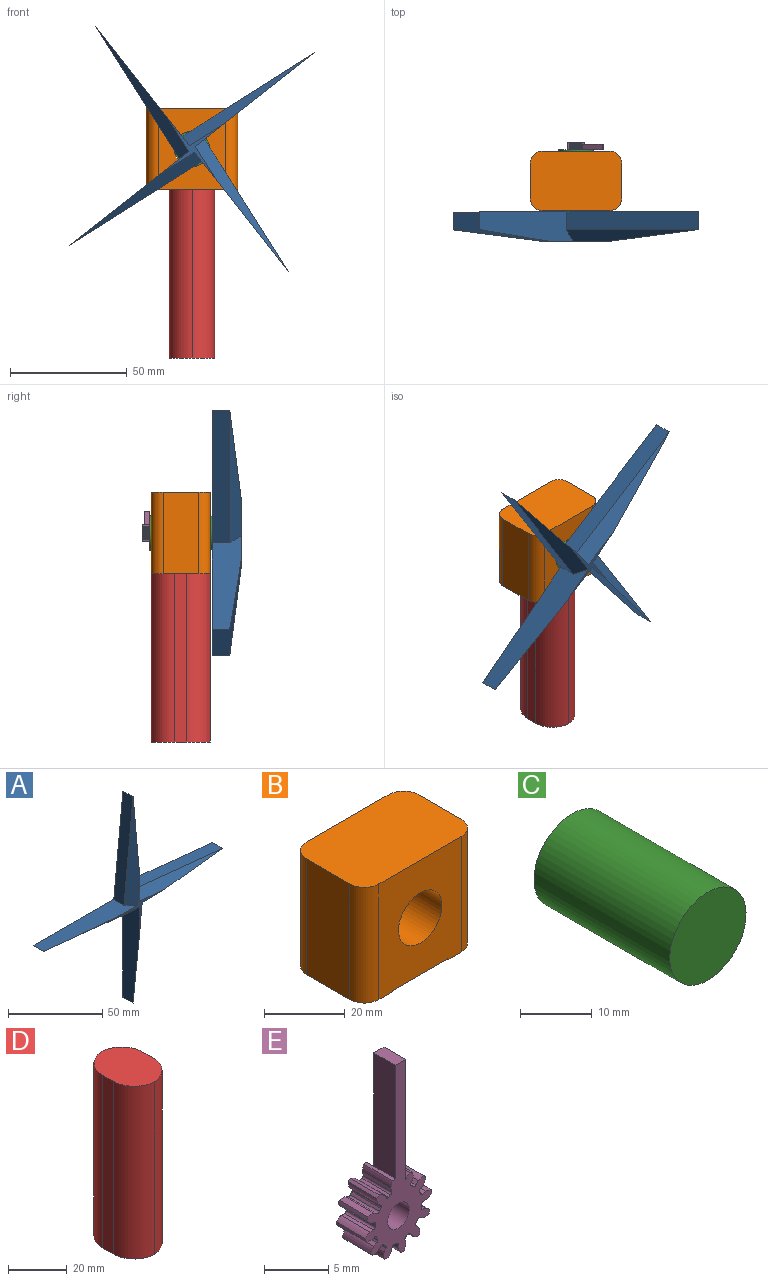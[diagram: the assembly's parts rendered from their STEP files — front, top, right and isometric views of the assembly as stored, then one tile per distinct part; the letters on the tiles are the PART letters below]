
ASSEMBLY  parts=5 mates=4
PART A: 14 faces, bbox 134x12.7x134 mm
  f0: plane 66.98x7.62mm, normal (-0.99,0,0.1), area 513.1mm2, adj f1,f7,f9,f13
  f1: plane 65.2x12.7mm, normal (0,0,1), area 650mm2, adj f0,f2,f8,f9,f12,f13
  f2: plane 66.98x7.62mm, normal (-0.1,0,-0.99), area 513.1mm2, adj f1,f3,f9,f12
  f3: plane 65.2x12.7mm, normal (-1,0,0), area 650mm2, adj f2,f4,f8,f9,f11,f12
  f4: plane 66.98x7.62mm, normal (0.99,0,-0.1), area 513.1mm2, adj f3,f5,f9,f11
  f5: plane 65.2x12.7mm, normal (0,0,-1), area 650mm2, adj f4,f6,f8,f9,f10,f11
  f6: plane 66.98x7.62mm, normal (0.1,0,0.99), area 513.1mm2, adj f5,f7,f9,f10
  f7: plane 65.2x12.7mm, normal (1,0,0), area 650mm2, adj f0,f6,f8,f9,f10,f13
  f8: plane 34.58x34.58mm, normal (0,-1,0), area 61.4mm2, adj f1,f3,f5,f7,f10,f11,f12,f13
  f9: plane 133.96x133.96mm, normal (0,1,0), area 922.1mm2, adj f0,f1,f2,f3,f4,f5,f6,f7
  f10: plane 66.98x6.88mm, normal (0.07,-0.71,0.7), area 304.3mm2, adj f5,f6,f7,f8
  f11: plane 66.98x6.88mm, normal (0.7,-0.71,-0.07), area 304.3mm2, adj f3,f4,f5,f8
  f12: plane 66.98x6.88mm, normal (-0.07,-0.71,-0.7), area 304.3mm2, adj f1,f2,f3,f8
  f13: plane 66.98x6.88mm, normal (-0.7,-0.71,0.07), area 304.3mm2, adj f0,f1,f7,f8
PART B: 15 faces, bbox 39.1x25.4x35.1 mm
  f0: plane 25.4x19.4mm, normal (0,0,-1), area 492.9mm2, adj f1,f7,f8,f9
  f1: plane 25.4x0.27mm, normal (-1,0,0), area 6.8mm2, adj f0,f2,f8,f9
  f2: plane 25.4x9.84mm, normal (0,0,-1), area 238.7mm2, adj f1,f3,f8,f9,f11,f13
  f3: plane 35.09x15.24mm, normal (1,0,0), area 534.7mm2, adj f2,f4,f11,f13
  f4: plane 39.07x25.4mm, normal (0,0,1), area 970.3mm2, adj f3,f5,f8,f9,f10,f11,f12,f13
  f5: plane 35.09x15.24mm, normal (-1,0,0), area 534.7mm2, adj f4,f6,f10,f12
  f6: plane 25.4x9.84mm, normal (0,0,-1), area 238.7mm2, adj f5,f7,f8,f9,f10,f12
  f7: plane 25.4x0.27mm, normal (1,0,0), area 6.8mm2, adj f0,f6,f8,f9
  f8: plane 35.09x28.91mm, normal (0,-1,0), area 827mm2, adj f0,f1,f2,f4,f6,f7,f12,f13
  f9: plane 35.09x28.91mm, normal (0,1,0), area 827mm2, adj f0,f1,f2,f4,f6,f7,f10,f11
  f10: cylinder r=5.08mm len=35.09mm, axis (0,0,-1), area 280mm2, adj f4,f5,f6,f9
  f11: cylinder r=5.08mm len=35.09mm, axis (0,0,1), area 280mm2, adj f2,f3,f4,f9
  f12: cylinder r=5.08mm len=35.09mm, axis (0,0,1), area 280mm2, adj f4,f5,f6,f8
  f13: cylinder r=5.08mm len=35.09mm, axis (0,0,-1), area 280mm2, adj f2,f3,f4,f8
  f14: cylinder r=7.62mm len=25.4mm, axis (0,-1,0), area 1216.1mm2, adj f8,f9
PART C: 3 faces, bbox 15x26.7x15 mm
  f0: cylinder r=7.49mm len=26.67mm, axis (0,1,0), area 1255.6mm2, adj f1,f2
  f1: plane 14.99x14.99mm, normal (0,-1,0), area 176.4mm2, adj f0
  f2: plane 14.99x14.99mm, normal (0,1,0), area 176.4mm2, adj f0
PART D: 8 faces, bbox 19.4x25.4x72.3 mm
  f0: plane 25.38x19.4mm, normal (0,0,-1), area 404.3mm2, adj f1,f3,f4,f5,f6,f7
  f1: plane 72.3x5.08mm, normal (1,0,0), area 367.3mm2, adj f0,f2,f5,f7
  f2: plane 25.38x19.4mm, normal (0,0,1), area 404.3mm2, adj f1,f3,f4,f5,f6,f7
  f3: plane 72.3x5.08mm, normal (-1,0,0), area 367.3mm2, adj f0,f2,f4,f6
  f4: cylinder r=10.16mm len=72.3mm, axis (0,0,-1), area 1120.7mm2, adj f0,f2,f3,f5
  f5: cylinder r=10.16mm len=72.3mm, axis (0,0,1), area 1120.7mm2, adj f0,f1,f2,f4
  f6: cylinder r=10.16mm len=72.3mm, axis (0,0,1), area 1120.7mm2, adj f0,f2,f3,f7
  f7: cylinder r=10.16mm len=72.3mm, axis (0,0,-1), area 1120.7mm2, adj f0,f1,f2,f6
PART E: 103 faces, bbox 7.4x3.2x18.2 mm
  f0: plane 0.79x0.37mm, normal (-0.97,0,0.26), area 0.3mm2, adj f2,f90,f97,f102
  f1: cylinder r=2.56mm len=0.79mm, axis (0,1,0), area 0.2mm2, adj f2,f5,f97,f102
  f2: cylinder r=0.2mm len=0.79mm, axis (0,1,0), area 0.2mm2, adj f0,f1,f97,f102
  f3: plane 0.79x0.38mm, normal (1,0,0), area 0.3mm2, adj f4,f5,f97,f102
  f4: extruded ~0.79x0.55mm, area 0.5mm2, adj f3,f93,f97,f102
  f5: cylinder r=0.2mm len=0.79mm, axis (0,1,0), area 0.2mm2, adj f1,f3,f97,f102
  f6: cylinder r=2.56mm len=3.18mm, axis (0,1,0), area 0.9mm2, adj f7,f16,f96,f97
  f7: cylinder r=0.2mm len=3.18mm, axis (0,1,0), area 1mm2, adj f6,f13,f96,f97
  f8: cylinder r=0.2mm len=3.18mm, axis (0,1,0), area 1mm2, adj f9,f92,f96,f97
  f9: plane 3.18x0.33mm, normal (0.87,0,0.5), area 1.2mm2, adj f8,f10,f96,f97
  f10: extruded ~3.18x0.56mm, area 2.1mm2, adj f9,f11,f96,f97
  f11: cylinder r=3.7mm len=3.18mm, axis (0,1,0), area 1mm2, adj f10,f12,f96,f97
  f12: extruded ~3.18x0.63mm, area 2.1mm2, adj f11,f13,f96,f97
  f13: plane 3.18x0.27mm, normal (-0.7,0,-0.71), area 1.2mm2, adj f7,f12,f96,f97
  f14: cylinder r=2.56mm len=3.18mm, axis (0,1,0), area 0.9mm2, adj f15,f24,f96,f97
  f15: cylinder r=0.2mm len=3.18mm, axis (0,1,0), area 1mm2, adj f14,f21,f96,f97
  f16: cylinder r=0.2mm len=3.18mm, axis (0,1,0), area 1mm2, adj f6,f17,f96,f97
  f17: plane 3.18x0.33mm, normal (0.5,0,0.86), area 1.2mm2, adj f16,f18,f96,f97
  f18: extruded ~3.18x0.64mm, area 2.1mm2, adj f17,f19,f96,f97
  f19: cylinder r=3.7mm len=3.18mm, axis (0,1,0), area 1mm2, adj f18,f20,f96,f97
  f20: extruded ~3.18x0.47mm, area 2.1mm2, adj f19,f21,f96,f97
  f21: plane 3.18x0.37mm, normal (-0.26,0,-0.97), area 1.2mm2, adj f15,f20,f96,f97
  f22: cylinder r=2.56mm len=3.18mm, axis (0,1,0), area 0.9mm2, adj f23,f32,f96,f97
  f23: cylinder r=0.2mm len=3.18mm, axis (0,1,0), area 1mm2, adj f22,f29,f96,f97
  f24: cylinder r=0.2mm len=3.18mm, axis (0,1,0), area 1mm2, adj f14,f25,f96,f97
  f25: plane 3.18x0.38mm, normal (0,0,1), area 1.2mm2, adj f24,f26,f96,f97
  f26: extruded ~3.18x0.55mm, area 2.1mm2, adj f25,f27,f96,f97
  f27: cylinder r=3.7mm len=3.18mm, axis (0,1,0), area 1mm2, adj f26,f28,f96,f97
  f28: extruded ~3.18x0.62mm, area 2.1mm2, adj f27,f29,f96,f97
  f29: plane 3.18x0.37mm, normal (0.26,0,-0.97), area 1.2mm2, adj f23,f28,f96,f97
  f30: cylinder r=2.56mm len=3.18mm, axis (0,1,0), area 0.9mm2, adj f31,f40,f96,f97
  f31: cylinder r=0.2mm len=3.18mm, axis (0,1,0), area 1mm2, adj f30,f37,f96,f97
  f32: cylinder r=0.2mm len=3.18mm, axis (0,1,0), area 1mm2, adj f22,f33,f96,f97
  f33: plane 3.18x0.33mm, normal (-0.5,0,0.87), area 1.2mm2, adj f32,f34,f96,f97
  f34: extruded ~3.18x0.56mm, area 2.1mm2, adj f33,f35,f96,f97
  f35: cylinder r=3.7mm len=3.18mm, axis (0,1,0), area 1mm2, adj f34,f36,f96,f97
  f36: extruded ~3.18x0.63mm, area 2.1mm2, adj f35,f37,f96,f97
  f37: plane 3.18x0.27mm, normal (0.71,0,-0.7), area 1.2mm2, adj f31,f36,f96,f97
  f38: cylinder r=2.56mm len=3.18mm, axis (0,1,0), area 0.9mm2, adj f39,f48,f96,f97
  f39: cylinder r=0.2mm len=3.18mm, axis (0,1,0), area 1mm2, adj f38,f45,f96,f97
  f40: cylinder r=0.2mm len=3.18mm, axis (0,1,0), area 1mm2, adj f30,f41,f96,f97
  f41: plane 3.18x0.33mm, normal (-0.86,0,0.5), area 1.2mm2, adj f40,f42,f96,f97
  f42: extruded ~3.18x0.64mm, area 2.1mm2, adj f41,f43,f96,f97
  f43: cylinder r=3.7mm len=3.18mm, axis (0,1,0), area 1mm2, adj f42,f44,f96,f97
  f44: extruded ~3.18x0.47mm, area 2.1mm2, adj f43,f45,f96,f97
  f45: plane 3.18x0.37mm, normal (0.97,0,-0.26), area 1.2mm2, adj f39,f44,f96,f97
  f46: cylinder r=2.56mm len=3.18mm, axis (0,1,0), area 0.9mm2, adj f47,f56,f96,f97
  f47: cylinder r=0.2mm len=3.18mm, axis (0,1,0), area 1mm2, adj f46,f53,f96,f97
  f48: cylinder r=0.2mm len=3.18mm, axis (0,1,0), area 1mm2, adj f38,f49,f96,f97
  f49: plane 3.18x0.38mm, normal (-1,0,0), area 1.2mm2, adj f48,f50,f96,f97
  f50: extruded ~3.18x0.55mm, area 2.1mm2, adj f49,f51,f96,f97
  f51: cylinder r=3.7mm len=3.18mm, axis (0,1,0), area 1mm2, adj f50,f52,f96,f97
  f52: extruded ~3.18x0.62mm, area 2.1mm2, adj f51,f53,f96,f97
  f53: plane 3.18x0.37mm, normal (0.97,0,0.26), area 1.2mm2, adj f47,f52,f96,f97
  f54: cylinder r=2.56mm len=3.18mm, axis (0,1,0), area 0.9mm2, adj f55,f64,f96,f97
  f55: cylinder r=0.2mm len=3.18mm, axis (0,1,0), area 1mm2, adj f54,f61,f96,f97
  f56: cylinder r=0.2mm len=3.18mm, axis (0,1,0), area 1mm2, adj f46,f57,f96,f97
  f57: plane 3.18x0.33mm, normal (-0.87,0,-0.5), area 1.2mm2, adj f56,f58,f96,f97
  f58: extruded ~3.18x0.56mm, area 2.1mm2, adj f57,f59,f96,f97
  f59: cylinder r=3.7mm len=3.18mm, axis (0,1,0), area 1mm2, adj f58,f60,f96,f97
  f60: extruded ~3.18x0.63mm, area 2.1mm2, adj f59,f61,f96,f97
  f61: plane 3.18x0.27mm, normal (0.7,0,0.71), area 1.2mm2, adj f55,f60,f96,f97
  f62: cylinder r=2.56mm len=3.18mm, axis (0,1,0), area 0.9mm2, adj f63,f72,f96,f97
  f63: cylinder r=0.2mm len=3.18mm, axis (0,1,0), area 1mm2, adj f62,f69,f96,f97
  f64: cylinder r=0.2mm len=3.18mm, axis (0,1,0), area 1mm2, adj f54,f65,f96,f97
  f65: plane 3.18x0.33mm, normal (-0.5,0,-0.86), area 1.2mm2, adj f64,f66,f96,f97
  f66: extruded ~3.18x0.64mm, area 2.1mm2, adj f65,f67,f96,f97
  f67: cylinder r=3.7mm len=3.18mm, axis (0,1,0), area 1mm2, adj f66,f68,f96,f97
  f68: extruded ~3.18x0.47mm, area 2.1mm2, adj f67,f69,f96,f97
  f69: plane 3.18x0.37mm, normal (0.26,0,0.97), area 1.2mm2, adj f63,f68,f96,f97
  f70: cylinder r=2.56mm len=3.18mm, axis (0,1,0), area 0.9mm2, adj f71,f80,f96,f97
  f71: cylinder r=0.2mm len=3.18mm, axis (0,1,0), area 1mm2, adj f70,f77,f96,f97
  f72: cylinder r=0.2mm len=3.18mm, axis (0,1,0), area 1mm2, adj f62,f73,f96,f97
  f73: plane 3.18x0.38mm, normal (0,0,-1), area 1.2mm2, adj f72,f74,f96,f97
  f74: extruded ~3.18x0.55mm, area 2.1mm2, adj f73,f75,f96,f97
  f75: cylinder r=3.7mm len=3.18mm, axis (0,1,0), area 1mm2, adj f74,f76,f96,f97
  f76: extruded ~3.18x0.62mm, area 2.1mm2, adj f75,f77,f96,f97
  f77: plane 3.18x0.37mm, normal (-0.26,0,0.97), area 1.2mm2, adj f71,f76,f96,f97
  f78: cylinder r=2.56mm len=3.18mm, axis (0,1,0), area 0.9mm2, adj f79,f86,f96,f97
  f79: cylinder r=0.2mm len=3.18mm, axis (0,1,0), area 1mm2, adj f78,f85,f96,f97
  f80: cylinder r=0.2mm len=3.18mm, axis (0,1,0), area 1mm2, adj f70,f81,f96,f97
  f81: plane 3.18x0.33mm, normal (0.5,0,-0.87), area 1.2mm2, adj f80,f82,f96,f97
  f82: extruded ~3.18x0.56mm, area 2.1mm2, adj f81,f83,f96,f97
  f83: cylinder r=3.7mm len=3.18mm, axis (0,1,0), area 1mm2, adj f82,f84,f96,f97
  f84: extruded ~3.18x0.63mm, area 2.1mm2, adj f83,f85,f96,f97
  f85: plane 3.18x0.27mm, normal (-0.71,0,0.7), area 1.2mm2, adj f79,f84,f96,f97
  f86: cylinder r=0.2mm len=3.18mm, axis (0,1,0), area 1mm2, adj f78,f87,f96,f97
  f87: plane 3.18x0.33mm, normal (0.86,0,-0.5), area 1.2mm2, adj f86,f88,f96,f97
  f88: extruded ~3.18x0.64mm, area 2.1mm2, adj f87,f89,f96,f97
  f89: cylinder r=3.7mm len=3.18mm, axis (0,1,0), area 1mm2, adj f88,f90,f96,f97
  f90: extruded ~3.18x0.47mm, area 2.1mm2, adj f0,f89,f96,f97,f100
  f91: plane 3.18x0.37mm, normal (-0.97,0,-0.26), area 1.2mm2, adj f94,f96,f97,f98
  f92: cylinder r=2.56mm len=3.18mm, axis (0,1,0), area 0.9mm2, adj f8,f96,f97,f98
  f93: cylinder r=3.7mm len=3.18mm, axis (0,1,0), area 1mm2, adj f4,f94,f96,f97,f99
  f94: extruded ~3.18x0.62mm, area 2.1mm2, adj f91,f93,f96,f97
  f95: cylinder r=1.19mm len=3.18mm, axis (0,1,0), area 23.8mm2, adj f96,f97
  f96: plane 18.2x7.38mm, normal (0,-1,0), area 39.1mm2, adj f6,f7,f8,f9,f10,f11,f12,f13
  f97: plane 7.38x7.38mm, normal (0,1,0), area 26mm2, adj f0,f1,f2,f3,f4,f5,f6,f7
  f98: cylinder r=0.2mm len=3.18mm, axis (0,1,0), area 1mm2, adj f91,f92,f96,f97
  f99: plane 10.82x2.39mm, normal (-1,0,0), area 25.8mm2, adj f93,f96,f101,f102
  f100: plane 11.47x2.39mm, normal (1,0,0), area 27.4mm2, adj f90,f96,f101,f102
  f101: plane 2.39x1.13mm, normal (0,0,1), area 2.7mm2, adj f96,f99,f100,f102
  f102: plane 11.99x1.13mm, normal (0,1,0), area 13.1mm2, adj f0,f1,f2,f3,f4,f5,f99,f100
PLACE A rot(axis=(0,1,0),51.9deg) t=(-28.56,-20.14,77.48)mm
PLACE B t=(-28.56,-0.45,23.93)mm
PLACE C rot(axis=(0,1,0),51.9deg) t=(-28.56,-0.45,77.48)mm
PLACE D t=(-28.56,-0.45,24.19)mm fixed
PLACE E rot(axis=(0,1,0),51.9deg) t=(-28.56,16.06,77.48)mm
MATE fastened C.f0 <-> A.f9  axis (0,-1,0) through (-28.56,-13.79,77.48)mm
MATE fastened D.f2 <-> B.f0  axis (0,0,1) through (-28.56,-0.45,60.21)mm
MATE fastened C.f0 <-> E.f1  axis (0,1,0) through (-28.56,12.88,77.48)mm
MATE revolute C.f0 <-> B.f14  axis (0,1,0) through (-28.56,-0.45,77.48)mm
